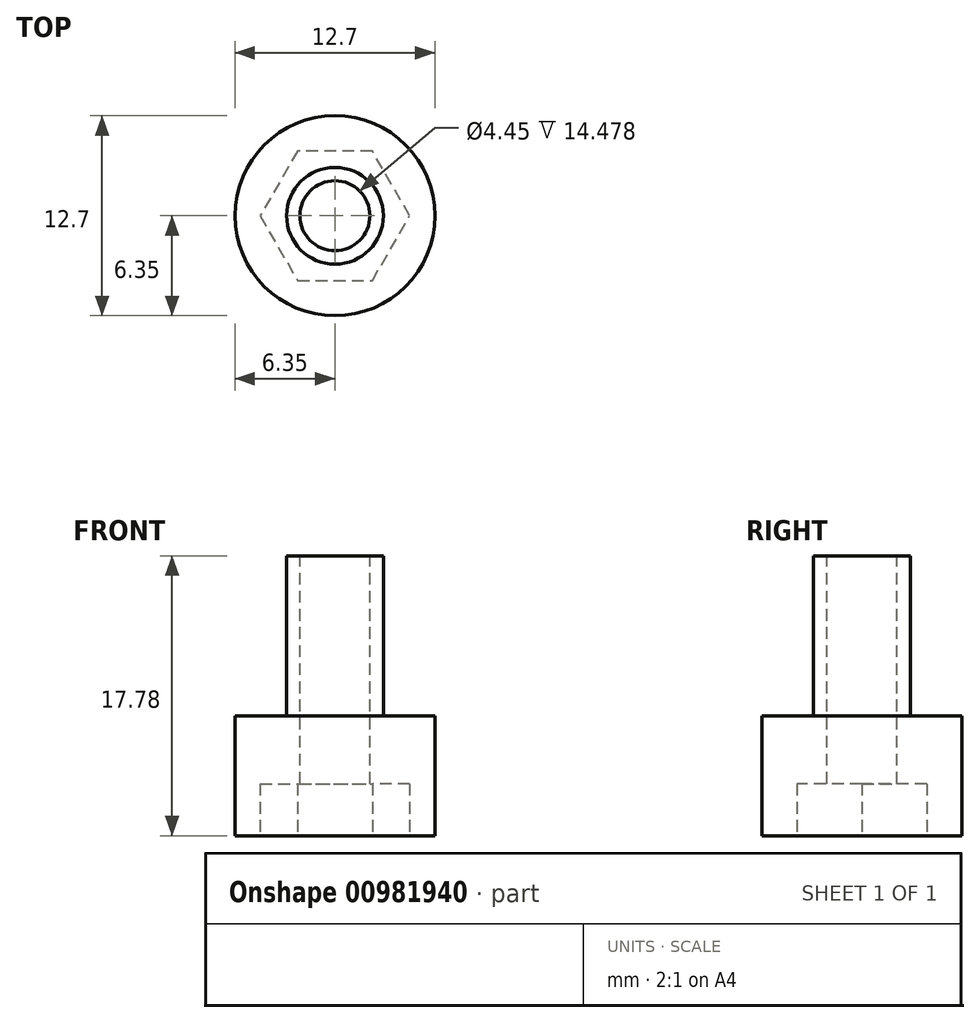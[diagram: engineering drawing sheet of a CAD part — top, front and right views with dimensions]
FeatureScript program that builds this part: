
annotation { "Feature Type Name" : "Feature", "Feature Type Description" : "" }
export const myFeature = defineFeature(function(context is Context, id is Id, definition is map)
    precondition{}
    {
        {
            var Q0;
            Q0=qCreatedBy(makeId("Top.planeOp"),FACE);
            var sketch = newSketch(context, id + "F0", { "sketchPlane" : qUnion([Q0])});
            skCircle(sketch, "E0", {"center": v(0, 0) * mm, "radius": 6.35 * mm});
            skSolve(sketch);
        }
        {
            var Q0;
            Q0=qSketchRegion(id+"F0",true);
            extrude(context, id + "F1", {"entities" : qUnion([Q0]), "depth" : 7.62 * mm, "offsetDistance" : 25.4 * mm});
        }
        {
            var Q0;
            Q0=makeQuery(id+"F1.opExtrude","CAP_FACE",FACE,{"disambiguationData":[OSD([sQuery(id+"F0.wireOp",EDGE,"E0")])],"isStart":false});
            var sketch = newSketch(context, id + "F2", { "sketchPlane" : qUnion([Q0])});
            skCircle(sketch, "E1", {"center": v(0, 0) * mm, "radius": 3.07 * mm});
            skSolve(sketch);
        }
        {
            var Q0;
            Q0=qSketchRegion(id+"F2",true);
            extrude(context, id + "F3", {"entities" : qUnion([Q0]), "operationType" : NewBodyOperationType.ADD, "depth" : 10.16 * mm, "offsetDistance" : 25.4 * mm});
        }
        {
            var Q0;
            Q0=makeQuery(id+"F3.opExtrude","CAP_FACE",FACE,{"disambiguationData":[OSD([sQuery(id+"F2.wireOp",EDGE,"E1")])],"isStart":false});
            var sketch = newSketch(context, id + "F4", { "sketchPlane" : qUnion([Q0])});
            skCircle(sketch, "E2", {"center": v(0, 0) * mm, "radius": 2.22 * mm});
            skSolve(sketch);
        }
        {
            var Q0;
            Q0=qSketchRegion(id+"F4",true);
            extrude(context, id + "F5", {"entities" : qUnion([Q0]), "operationType" : NewBodyOperationType.REMOVE, "endBound" : BoundingType.THROUGH_ALL, "oppositeDirection" : true, "depth" : 25.4 * mm, "offsetDistance" : 25.4 * mm});
        }
        {
            var Q0;
            Q0=makeQuery(id+"F1.opExtrude","CAP_FACE",FACE,{"disambiguationData":[OSD([sQuery(id+"F0.wireOp",EDGE,"E0")])],"isStart":true});
            var sketch = newSketch(context, id + "F6", { "sketchPlane" : qUnion([Q0])});
            skCircle(sketch, "E3.cCircle", {"center": v(0, 0) * mm, "radius": 4.11 * mm, "construction": true});
            skLineSegment(sketch, "E3.0", {"start": v(-2.37, 4.11) * mm, "end": v(2.37, 4.11) * mm});
            skLineSegment(sketch, "E3.1", {"start": v(2.37, 4.11) * mm, "end": v(4.75, 0) * mm});
            skLineSegment(sketch, "E3.2", {"start": v(4.75, 0) * mm, "end": v(2.37, -4.11) * mm});
            skLineSegment(sketch, "E3.3", {"start": v(2.37, -4.11) * mm, "end": v(-2.37, -4.11) * mm});
            skLineSegment(sketch, "E3.4", {"start": v(-2.37, -4.11) * mm, "end": v(-4.75, 0) * mm});
            skLineSegment(sketch, "E3.5", {"start": v(-4.75, 0) * mm, "end": v(-2.37, 4.11) * mm});
            skPoint(sketch, "E3.0.midPoint", {"position": v(0, 4.11) * mm});
            skSolve(sketch);
        }
        {
            var Q0;
            Q0=qSketchRegion(id+"F6",true);
            extrude(context, id + "F7", {"entities" : qUnion([Q0]), "operationType" : NewBodyOperationType.REMOVE, "oppositeDirection" : true, "depth" : 3.3 * mm, "offsetDistance" : 25.4 * mm});
        }
    });
